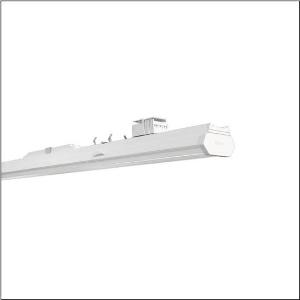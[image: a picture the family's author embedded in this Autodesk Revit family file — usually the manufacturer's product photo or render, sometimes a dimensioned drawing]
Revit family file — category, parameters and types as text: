
# Revit family: licross_r__21_protected_mo_52td127n485g_89bf
name_source: partatom
category: Lighting Fixtures
units: mm (PartAtom-declared; Revit-internal decimal feet)

## family parameters
Cut with Voids When Loaded = No
Host = Face
Light Source = No
Part Type = Normal
Room Calculation Point = No
Round Connector Dimension = Use Diameter
Shared = No

## types (1)
- Licross® 21 Protected MO (1 x LED, 8610 lm, 47.9 W, 4000K)
    Apparent Load = 48 VA
    CIE Flux Codes = 73 92 98 99 100
    Color Rendering = 80
    Color Temperature = 4000K
    Default Elevation = 1800 mm
    Description = Licross® 21 Protected MO, luminaire insert, of sheet steel, galvanised, coil coated, white, length: 1.500mm, width: 90mm, height: 101mm, LED rated luminous flux: 8.610lm, light colour: 840, control gear: ON/OFF, with plug, 3-pole, with phase selection, mains connection: 220..240V, AC, 50/60Hz, rated input power: 48W, halogen-free wiring, primary light control with lens, of plastic, primary optical cover: cover, of PMMA, light emission: direct distribution, primary light characteristic: symmetric, protection rating (complete): IP54, insulation class (complete): insulation class I (protective earthing), certification: CE, ENEC, VDE, UKCA, protection symbol: D if used in an environment with non-conductive dust loads with corresponding accessories, impact resistance: IK06, permissible ambient temperature for indoor applications: -35..+45°C, corresponds to IFS (International Featured Standards) requirements for safety and quality in the food industry, reducing of maximum allowable ambient temperature of 5°C with ceiling mounting, LABS conformity tested according to VDMA 24364:2018-05, packaging unit: 1 piece
    Height = 92 mm
    Lamp = 1 x LED
    Lamp Light Flux = 8610 lm
    Lamp Power = 47.9 W
    Lamp count = 1
    Length = 1500 mm
    Luminous efficacy = 180 lm/W
    Manufacturer = Siteco
    ModVariant = No
    Model = 52TD127N485G
    Mounting Place = Ceiling
    Mounting Type = Pendant
    Number of Poles = 1
    OnlyDefault = Yes
    Power Factor = 1
    Product Name = Licross® 21 Protected MO
    Product group = luminaire insert
    ProductGroupID = 901
    Protection Class = Protection class I
    Protection Degree = IP 54
    RLX_Detail_Level = 1
    RLX_Emergency_Light_Flux = 0 lm
    RLX_Emergency_Type = 0
    RLX_Emergency_Type_DB = No
    RlxData = <blob elided: 20649 chars, md5=fbca5836>
    Socket = socket
    Standby Power = 0 W
    System Light Flux = 8610 lm
    System Power = 48 W
    Type Comments = Product without accessories
    Type Image = l_1256148.jpg
    URL = http://relux.com
    VarID = ---
    Voltage = 0 V
    Weight = 0.00 kg
    Width = 88 mm

## geometry (parser evidence)
native form markers: Blend x4, Sweep x11
no freeform markers — native parametric forms only
